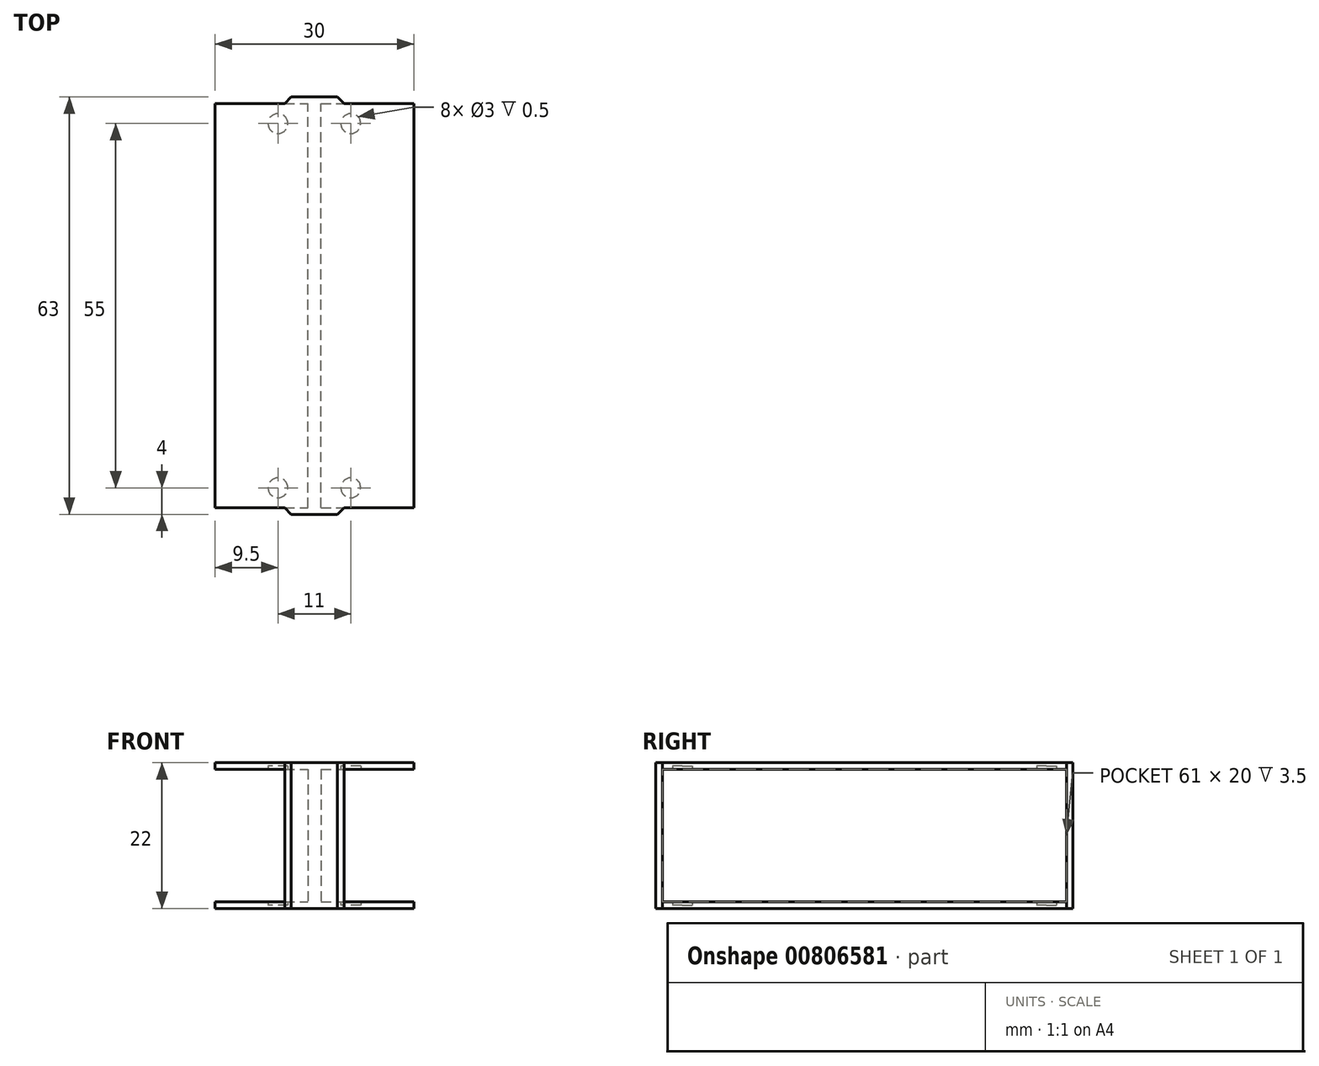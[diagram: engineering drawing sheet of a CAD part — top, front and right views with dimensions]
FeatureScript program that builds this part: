
annotation { "Feature Type Name" : "Feature", "Feature Type Description" : "" }
export const myFeature = defineFeature(function(context is Context, id is Id, definition is map)
    precondition{}
    {
        {
            var Q0;
            Q0=qCreatedBy(makeId("Top.planeOp"),FACE);
            var sketch = newSketch(context, id + "F0", { "sketchPlane" : qUnion([Q0])});
            skLineSegment(sketch, "E0.bottom", {"start": v(-15, 30.5) * mm, "end": v(15, 30.5) * mm});
            skLineSegment(sketch, "E0.top", {"start": v(-15, -30.5) * mm, "end": v(15, -30.5) * mm});
            skLineSegment(sketch, "E0.left", {"start": v(-15, 30.5) * mm, "end": v(-15, -30.5) * mm});
            skLineSegment(sketch, "E0.right", {"start": v(15, 30.5) * mm, "end": v(15, -30.5) * mm});
            skCircle(sketch, "E1", {"center": v(-5.5, 27.5) * mm, "radius": 1.5 * mm});
            skCircle(sketch, "E2", {"center": v(5.5, 27.5) * mm, "radius": 1.5 * mm});
            skCircle(sketch, "E3", {"center": v(5.5, -27.5) * mm, "radius": 1.5 * mm});
            skCircle(sketch, "E4", {"center": v(-5.5, -27.5) * mm, "radius": 1.5 * mm});
            skLineSegment(sketch, "E5", {"start": v(-4.5, -30.5) * mm, "end": v(-3.5, -31.5) * mm});
            skLineSegment(sketch, "E6", {"start": v(-3.5, -31.5) * mm, "end": v(3.5, -31.5) * mm});
            skLineSegment(sketch, "E7", {"start": v(3.5, -31.5) * mm, "end": v(4.5, -30.5) * mm});
            skLineSegment(sketch, "E8", {"start": v(-4.5, 30.5) * mm, "end": v(-3.5, 31.5) * mm});
            skLineSegment(sketch, "E9", {"start": v(-3.5, 31.5) * mm, "end": v(3.5, 31.5) * mm});
            skLineSegment(sketch, "E10", {"start": v(3.5, 31.5) * mm, "end": v(4.5, 30.5) * mm});
            skSolve(sketch);
        }
        {
            var Q0;
            Q0=makeQuery(id+"F0.imprint","IMPRINT",FACE,{"disambiguationData":[TD([[makeQuery(id+"F0.imprint","IMPRINT",EDGE,{"derivedFrom":sQuery(id+"F0.wireOp",EDGE,"E0.bottom")}),-1.0]])]});
            var Q1;
            Q1=makeQuery(id+"F0.imprint","IMPRINT",FACE,{"disambiguationData":[TD([[makeQuery(id+"F0.imprint","IMPRINT",EDGE,{"derivedFrom":sQuery(id+"F0.wireOp",EDGE,"E3")}),1.0]])]});
            var Q2;
            Q2=makeQuery(id+"F0.imprint","IMPRINT",FACE,{"disambiguationData":[TD([[makeQuery(id+"F0.imprint","IMPRINT",EDGE,{"derivedFrom":sQuery(id+"F0.wireOp",EDGE,"E4")}),1.0]])]});
            var Q3;
            Q3=makeQuery(id+"F0.imprint","IMPRINT",FACE,{"disambiguationData":[TD([[makeQuery(id+"F0.imprint","IMPRINT",EDGE,{"derivedFrom":sQuery(id+"F0.wireOp",EDGE,"E1")}),1.0]])]});
            var Q4;
            Q4=makeQuery(id+"F0.imprint","IMPRINT",FACE,{"disambiguationData":[TD([[makeQuery(id+"F0.imprint","IMPRINT",EDGE,{"derivedFrom":sQuery(id+"F0.wireOp",EDGE,"E2")}),1.0]])]});
            var Q5;
            {var subQ0=sQuery(id+"F0.wireOp",EDGE,"E8");Q5=makeQuery(id+"F0.imprint","IMPRINT",FACE,{"disambiguationData":[TD([[makeQuery(id+"F0.imprint","IMPRINT",EDGE,{"derivedFrom":subQ0}),-1.0]])]});}
            var Q6;
            {var subQ0=sQuery(id+"F0.wireOp",EDGE,"E5");Q6=makeQuery(id+"F0.imprint","IMPRINT",FACE,{"disambiguationData":[TD([[makeQuery(id+"F0.imprint","IMPRINT",EDGE,{"derivedFrom":subQ0}),1.0]])]});}
            extrude(context, id + "F1", {"entities" : qUnion([Q0, Q1, Q2, Q3, Q4, Q5, Q6]), "endBound" : BoundingType.SYMMETRIC, "depth" : 22 * mm, "offsetDistance" : 25 * mm});
        }
        {
            var Q0;
            Q0=qCreatedBy(makeId("Right.planeOp"),FACE);
            var sketch = newSketch(context, id + "F2", { "sketchPlane" : qUnion([Q0])});
            skLineSegment(sketch, "E11.bottom", {"start": v(-30.5, 10) * mm, "end": v(30.5, 10) * mm});
            skLineSegment(sketch, "E11.top", {"start": v(-30.5, -10) * mm, "end": v(30.5, -10) * mm});
            skLineSegment(sketch, "E11.left", {"start": v(-30.5, 10) * mm, "end": v(-30.5, -10) * mm});
            skLineSegment(sketch, "E11.right", {"start": v(30.5, 10) * mm, "end": v(30.5, -10) * mm});
            skLineSegment(sketch, "E12", {"start": v(-30.5, 9) * mm, "end": v(30.5, 9) * mm});
            skLineSegment(sketch, "E13", {"start": v(-30.5, -9) * mm, "end": v(30.5, -9) * mm});
            skSolve(sketch);
        }
        {
            var Q0;
            {var subQ0=sQuery(id+"F2.wireOp",EDGE,"E11.bottom");Q0=makeQuery(id+"F2.imprint","IMPRINT",FACE,{"disambiguationData":[TD([[makeQuery(id+"F2.imprint","IMPRINT",EDGE,{"derivedFrom":subQ0}),-1.0]])]});}
            var Q1;
            {var subQ0=sQuery(id+"F2.wireOp",EDGE,"E12");Q1=makeQuery(id+"F2.imprint","IMPRINT",FACE,{"disambiguationData":[TD([[makeQuery(id+"F2.imprint","IMPRINT",EDGE,{"derivedFrom":subQ0}),-1.0]])]});}
            var Q2;
            {var subQ0=sQuery(id+"F2.wireOp",EDGE,"E11.top");Q2=makeQuery(id+"F2.imprint","IMPRINT",FACE,{"disambiguationData":[TD([[makeQuery(id+"F2.imprint","IMPRINT",EDGE,{"derivedFrom":subQ0}),1.0]])]});}
            extrude(context, id + "F3", {"entities" : qUnion([Q0, Q1, Q2]), "operationType" : NewBodyOperationType.REMOVE, "endBound" : BoundingType.SYMMETRIC, "oppositeDirection" : true, "depth" : 30 * mm, "offsetDistance" : 25 * mm});
        }
        {
            var Q0;
            {var subQ0=sQuery(id+"F2.wireOp",EDGE,"E11.bottom");Q0=makeQuery(id+"F2.imprint","IMPRINT",FACE,{"disambiguationData":[TD([[makeQuery(id+"F2.imprint","IMPRINT",EDGE,{"derivedFrom":subQ0}),-1.0]])]});}
            var Q1;
            {var subQ0=sQuery(id+"F2.wireOp",EDGE,"E12");Q1=makeQuery(id+"F2.imprint","IMPRINT",FACE,{"disambiguationData":[TD([[makeQuery(id+"F2.imprint","IMPRINT",EDGE,{"derivedFrom":subQ0}),-1.0]])]});}
            var Q2;
            {var subQ0=sQuery(id+"F2.wireOp",EDGE,"E11.top");Q2=makeQuery(id+"F2.imprint","IMPRINT",FACE,{"disambiguationData":[TD([[makeQuery(id+"F2.imprint","IMPRINT",EDGE,{"derivedFrom":subQ0}),1.0]])]});}
            extrude(context, id + "F4", {"entities" : qUnion([Q0, Q1, Q2]), "operationType" : NewBodyOperationType.ADD, "endBound" : BoundingType.SYMMETRIC, "depth" : 2 * mm, "offsetDistance" : 25 * mm});
        }
        {
            var Q0;
            Q0=makeQuery(id+"F0.imprint","IMPRINT",FACE,{"disambiguationData":[TD([[makeQuery(id+"F0.imprint","IMPRINT",EDGE,{"derivedFrom":sQuery(id+"F0.wireOp",EDGE,"E4")}),1.0]])]});
            var Q1;
            Q1=makeQuery(id+"F0.imprint","IMPRINT",FACE,{"disambiguationData":[TD([[makeQuery(id+"F0.imprint","IMPRINT",EDGE,{"derivedFrom":sQuery(id+"F0.wireOp",EDGE,"E3")}),1.0]])]});
            var Q2;
            Q2=makeQuery(id+"F0.imprint","IMPRINT",FACE,{"disambiguationData":[TD([[makeQuery(id+"F0.imprint","IMPRINT",EDGE,{"derivedFrom":sQuery(id+"F0.wireOp",EDGE,"E2")}),1.0]])]});
            var Q3;
            Q3=makeQuery(id+"F0.imprint","IMPRINT",FACE,{"disambiguationData":[TD([[makeQuery(id+"F0.imprint","IMPRINT",EDGE,{"derivedFrom":sQuery(id+"F0.wireOp",EDGE,"E1")}),1.0]])]});
            extrude(context, id + "F5", {"entities" : qUnion([Q0, Q1, Q2, Q3]), "operationType" : NewBodyOperationType.REMOVE, "endBound" : BoundingType.SYMMETRIC, "depth" : 21 * mm, "offsetDistance" : 25 * mm});
        }
    });
